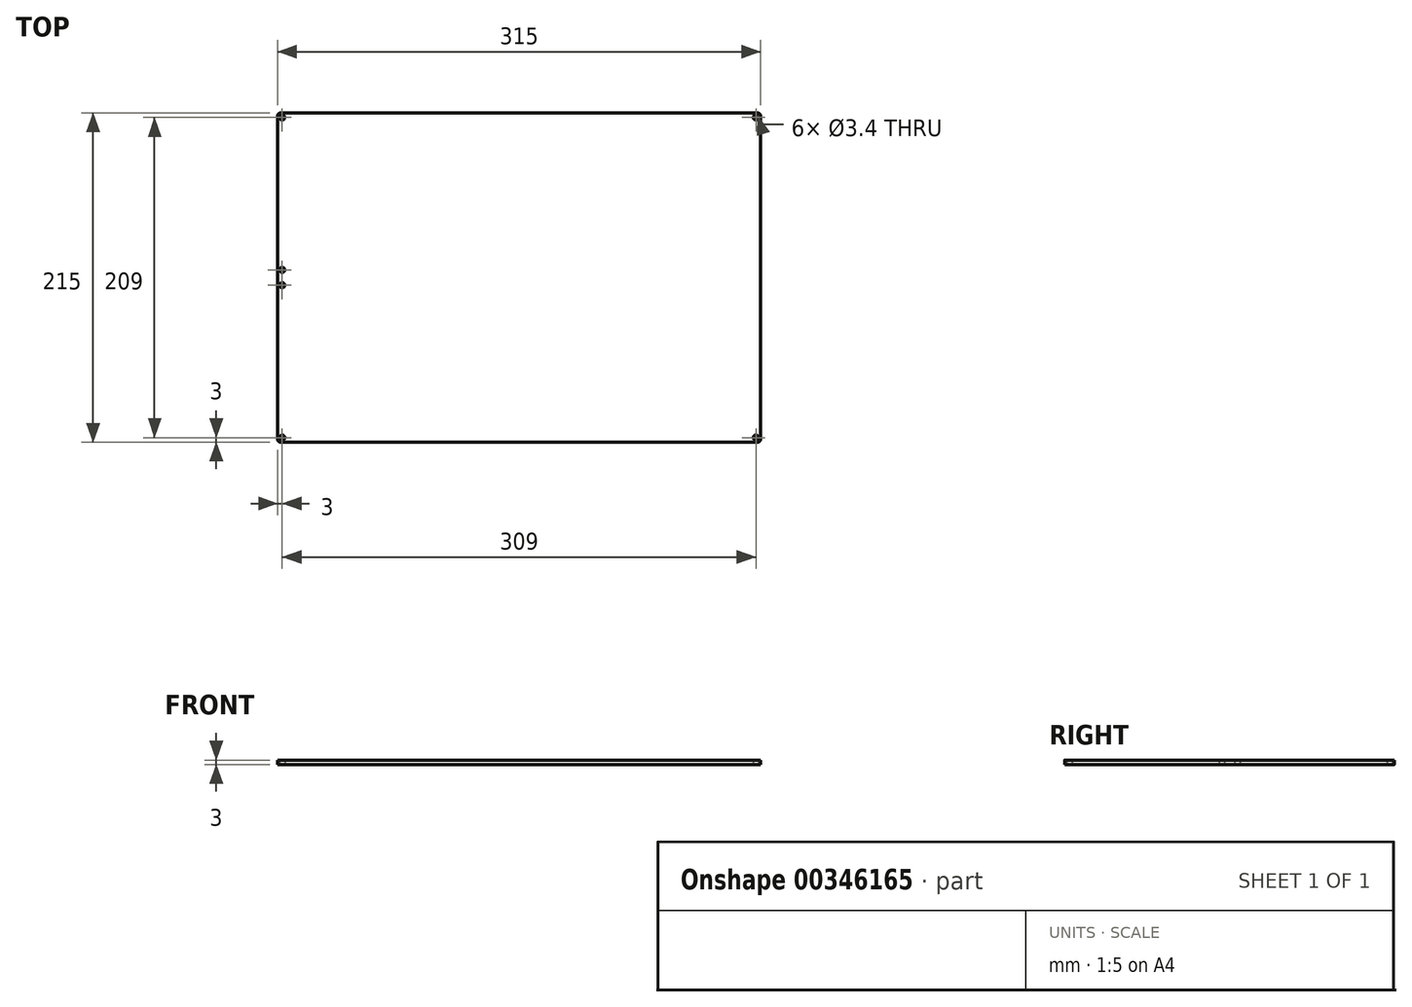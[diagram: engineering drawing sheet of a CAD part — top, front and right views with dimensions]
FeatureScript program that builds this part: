
annotation { "Feature Type Name" : "Feature", "Feature Type Description" : "" }
export const myFeature = defineFeature(function(context is Context, id is Id, definition is map)
    precondition{}
    {
        {
            var Q0;
            Q0=qCreatedBy(makeId("Top.planeOp"),FACE);
            var sketch = newSketch(context, id + "F0", { "sketchPlane" : qUnion([Q0])});
            skLineSegment(sketch, "E0.bottom", {"start": v(-155.5, 107.5) * mm, "end": v(155.5, 107.5) * mm});
            skLineSegment(sketch, "E0.top", {"start": v(-155.5, -107.5) * mm, "end": v(155.5, -107.5) * mm});
            skLineSegment(sketch, "E0.left", {"start": v(157.5, 105.5) * mm, "end": v(157.5, -105.5) * mm});
            skLineSegment(sketch, "E0.right", {"start": v(-157.5, 105.5) * mm, "end": v(-157.5, -105.5) * mm});
            skLineSegment(sketch, "E1.bottom", {"start": v(-154.5, 104.5) * mm, "end": v(154.5, 104.5) * mm, "construction": true});
            skLineSegment(sketch, "E1.top", {"start": v(-154.5, -104.5) * mm, "end": v(154.5, -104.5) * mm, "construction": true});
            skLineSegment(sketch, "E1.left", {"start": v(154.5, 104.5) * mm, "end": v(154.5, -104.5) * mm, "construction": true});
            skLineSegment(sketch, "E1.right", {"start": v(-154.5, 104.5) * mm, "end": v(-154.5, -104.5) * mm, "construction": true});
            skPoint(sketch, "E2", {"position": v(0, 104.5) * mm});
            skPoint(sketch, "E2.positionSnap0", {"position": v(0, 107.5) * mm});
            skPoint(sketch, "E3", {"position": v(-157.5, 0) * mm});
            skPoint(sketch, "E4", {"position": v(-154.5, 0) * mm});
            skCircle(sketch, "E5", {"center": v(-154.5, 104.5) * mm, "radius": 1.7 * mm});
            skCircle(sketch, "E6", {"center": v(154.5, 104.5) * mm, "radius": 1.7 * mm});
            skCircle(sketch, "E7", {"center": v(154.5, -104.5) * mm, "radius": 1.7 * mm});
            skCircle(sketch, "E8", {"center": v(-154.5, -104.5) * mm, "radius": 1.7 * mm});
            skCircle(sketch, "E9", {"center": v(-154.5, 5) * mm, "radius": 1.7 * mm});
            skCircle(sketch, "E10", {"center": v(-154.5, -5) * mm, "radius": 1.7 * mm});
            skLineSegment(sketch, "E11", {"start": v(-154.5, 5) * mm, "end": v(-154.5, -5) * mm, "construction": true});
            skPoint(sketch, "E12.visualSharp", {"position": v(-157.5, 107.5) * mm});
            skArc(sketch, "E12.filletArc", {"start": v(-155.5, 107.5) * mm, "mid": v(-156.91, 106.91) * mm, "end": v(-157.5, 105.5) * mm});
            skPoint(sketch, "E13.visualSharp", {"position": v(157.5, 107.5) * mm});
            skArc(sketch, "E13.filletArc", {"start": v(157.5, 105.5) * mm, "mid": v(156.91, 106.91) * mm, "end": v(155.5, 107.5) * mm});
            skPoint(sketch, "E14.visualSharp", {"position": v(157.5, -107.5) * mm});
            skArc(sketch, "E14.filletArc", {"start": v(155.5, -107.5) * mm, "mid": v(156.91, -106.91) * mm, "end": v(157.5, -105.5) * mm});
            skPoint(sketch, "E15.visualSharp", {"position": v(-157.5, -107.5) * mm});
            skArc(sketch, "E15.filletArc", {"start": v(-157.5, -105.5) * mm, "mid": v(-156.91, -106.91) * mm, "end": v(-155.5, -107.5) * mm});
            skSolve(sketch);
        }
        {
            var Q0;
            Q0=makeQuery(id+"F0.imprint","IMPRINT",FACE,{"disambiguationData":[TD([[makeQuery(id+"F0.imprint","IMPRINT",EDGE,{"derivedFrom":sQuery(id+"F0.wireOp",EDGE,"E0.bottom")}),-1.0]])]});
            extrude(context, id + "F1", {"entities" : qUnion([Q0]), "depth" : 3 * mm});
        }
    });
